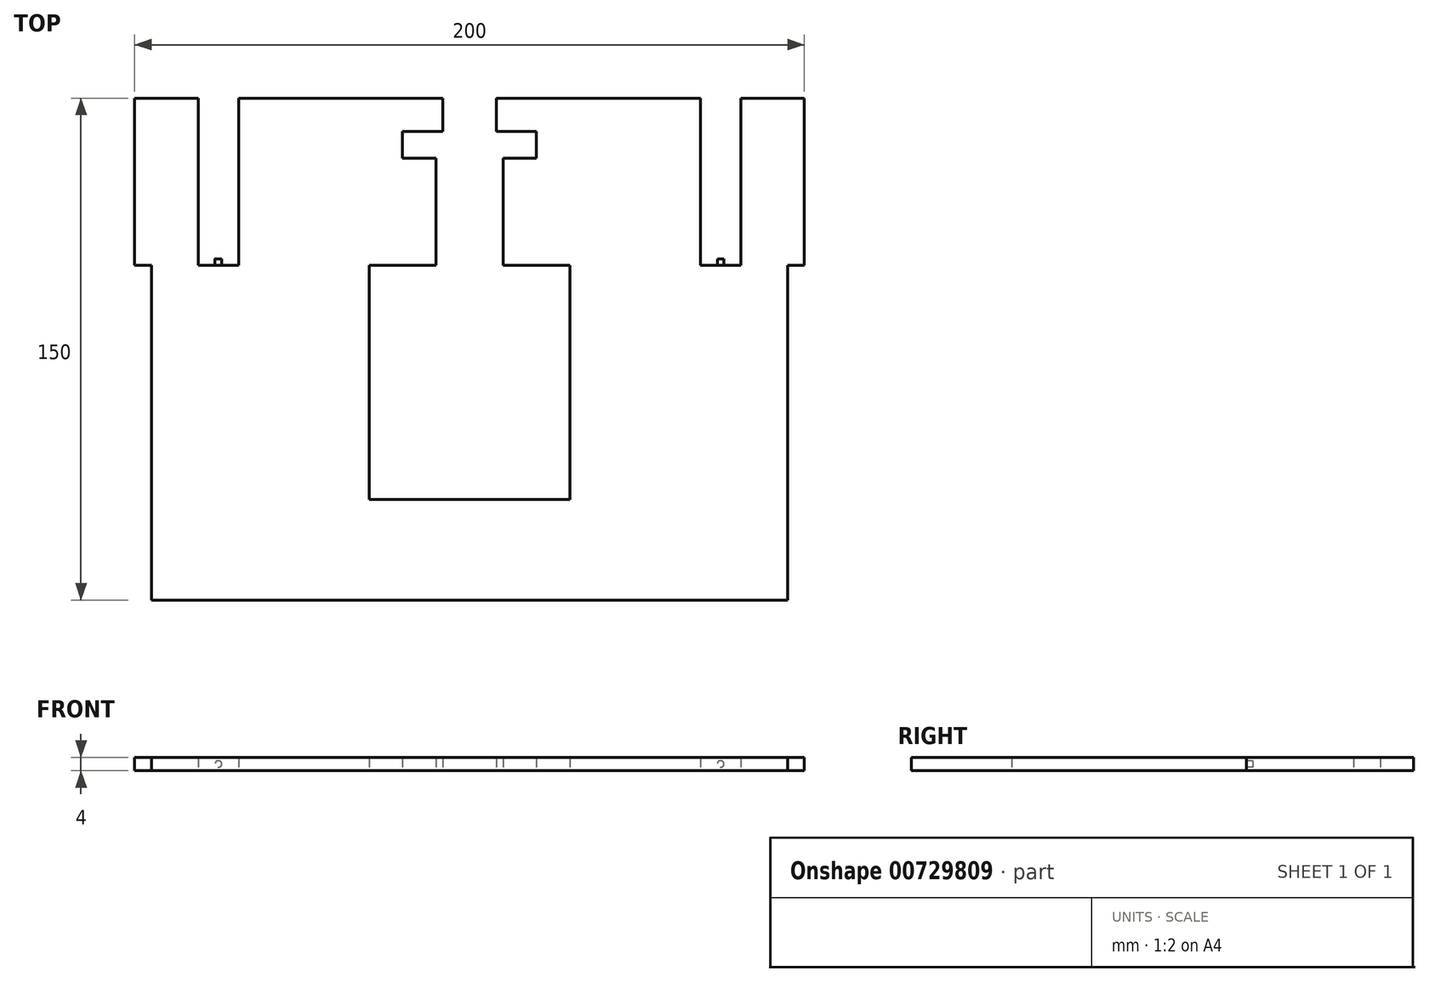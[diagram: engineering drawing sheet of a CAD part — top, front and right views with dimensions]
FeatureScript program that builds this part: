
annotation { "Feature Type Name" : "Feature", "Feature Type Description" : "" }
export const myFeature = defineFeature(function(context is Context, id is Id, definition is map)
    precondition{}
    {
        {
            var Q0;
            Q0=qCreatedBy(makeId("Top.planeOp"),FACE);
            var sketch = newSketch(context, id + "F0", { "sketchPlane" : qUnion([Q0])});
            skLineSegment(sketch, "E0.top", {"start": v(0, 50) * mm, "end": v(150, 50) * mm, "construction": true});
            skLineSegment(sketch, "E0.left", {"start": v(0, 0) * mm, "end": v(0, 50) * mm, "construction": true});
            skLineSegment(sketch, "E0.right", {"start": v(150, 0) * mm, "end": v(150, 50) * mm, "construction": true});
            skLineSegment(sketch, "E1.0", {"start": v(-6, 0) * mm, "end": v(-6, 50) * mm});
            skLineSegment(sketch, "E2.0", {"start": v(6, 0) * mm, "end": v(6, 50) * mm});
            skLineSegment(sketch, "E3.0", {"start": v(156, 0) * mm, "end": v(156, 50) * mm});
            skLineSegment(sketch, "E4.0", {"start": v(144, 0) * mm, "end": v(144, 50) * mm});
            skLineSegment(sketch, "E5", {"start": v(-6, 0) * mm, "end": v(6, 0) * mm});
            skLineSegment(sketch, "E6", {"start": v(144, 0) * mm, "end": v(156, 0) * mm});
            skLineSegment(sketch, "E7", {"start": v(156, 50) * mm, "end": v(175, 50) * mm});
            skLineSegment(sketch, "E8", {"start": v(175, 50) * mm, "end": v(175, 0) * mm});
            skLineSegment(sketch, "E9", {"start": v(170, -100) * mm, "end": v(-20, -100) * mm});
            skLineSegment(sketch, "E10", {"start": v(-25, 50) * mm, "end": v(-6, 50) * mm});
            skLineSegment(sketch, "E11", {"start": v(6, 50) * mm, "end": v(67, 50) * mm});
            skLineSegment(sketch, "E12", {"start": v(65, 0) * mm, "end": v(45, 0) * mm});
            skLineSegment(sketch, "E13", {"start": v(45, 0) * mm, "end": v(45, -70) * mm});
            skLineSegment(sketch, "E14", {"start": v(45, -70) * mm, "end": v(105, -70) * mm});
            skLineSegment(sketch, "E15", {"start": v(105, -70) * mm, "end": v(105, 0) * mm});
            skLineSegment(sketch, "E16", {"start": v(83, 50) * mm, "end": v(144, 50) * mm});
            skLineSegment(sketch, "E17", {"start": v(75, -70) * mm, "end": v(75, 50) * mm, "construction": true});
            skLineSegment(sketch, "E18.0", {"start": v(85, 0) * mm, "end": v(85, 32) * mm});
            skLineSegment(sketch, "E19.0", {"start": v(65, 0) * mm, "end": v(65, 32) * mm});
            skLineSegment(sketch, "E20", {"start": v(85, 0) * mm, "end": v(105, 0) * mm});
            skLineSegment(sketch, "E21", {"start": v(67, 40) * mm, "end": v(55, 40) * mm});
            skLineSegment(sketch, "E22", {"start": v(55, 40) * mm, "end": v(55, 32) * mm});
            skLineSegment(sketch, "E23", {"start": v(55, 32) * mm, "end": v(65, 32) * mm});
            skLineSegment(sketch, "E24", {"start": v(85, 32) * mm, "end": v(95, 32) * mm});
            skLineSegment(sketch, "E25", {"start": v(95, 32) * mm, "end": v(95, 40) * mm});
            skLineSegment(sketch, "E26", {"start": v(95, 40) * mm, "end": v(83, 40) * mm});
            skLineSegment(sketch, "E27", {"start": v(67, 50) * mm, "end": v(67, 40) * mm});
            skLineSegment(sketch, "E28", {"start": v(83, 50) * mm, "end": v(83, 40) * mm});
            skLineSegment(sketch, "E29", {"start": v(67, 50) * mm, "end": v(75, 50) * mm, "construction": true});
            skLineSegment(sketch, "E30", {"start": v(83, 50) * mm, "end": v(75, 50) * mm, "construction": true});
            skLineSegment(sketch, "E31", {"start": v(-25, 0) * mm, "end": v(-25, 50) * mm});
            skLineSegment(sketch, "E32", {"start": v(-20, 0) * mm, "end": v(-20, -100) * mm});
            skLineSegment(sketch, "E33", {"start": v(170, -100) * mm, "end": v(170, 0) * mm});
            skLineSegment(sketch, "E34", {"start": v(170, 0) * mm, "end": v(175, 0) * mm});
            skLineSegment(sketch, "E35", {"start": v(-25, 0) * mm, "end": v(-20, 0) * mm});
            skSolve(sketch);
        }
        {
            var Q0;
            Q0 = qSketchRegion(id + "F0", true);
            extrude(context, id + "F1", {"entities" : qUnion([Q0]), "depth" : 2 * mm, "offsetDistance" : 25 * mm, "hasSecondDirection" : true, "secondDirectionOppositeDirection" : true, "secondDirectionDepth" : 2 * mm});
        }
        {
            var Q0;
            Q0=makeQuery(id+"F1.opExtrude","SWEPT_FACE",FACE,{"disambiguationData":[OSD([sQuery(id+"F0.wireOp",EDGE,"E6")])]});
            var sketch = newSketch(context, id + "F2", { "sketchPlane" : qUnion([Q0])});
            skLineSegment(sketch, "E36", {"start": v(-144, 0) * mm, "end": v(-150, 0) * mm, "construction": true});
            skLineSegment(sketch, "E37", {"start": v(-150, 0) * mm, "end": v(-150, 2) * mm, "construction": true});
            skCircle(sketch, "E38", {"center": v(-150, 0) * mm, "radius": 1 * mm});
            skCircle(sketch, "E39", {"center": v(0, 0) * mm, "radius": 1 * mm});
            skSolve(sketch);
        }
        {
            var Q0;
            Q0 = qSketchRegion(id + "F2", true);
            extrude(context, id + "F3", {"entities" : qUnion([Q0]), "operationType" : NewBodyOperationType.ADD, "depth" : 2 * mm, "offsetDistance" : 25 * mm});
        }
    });
